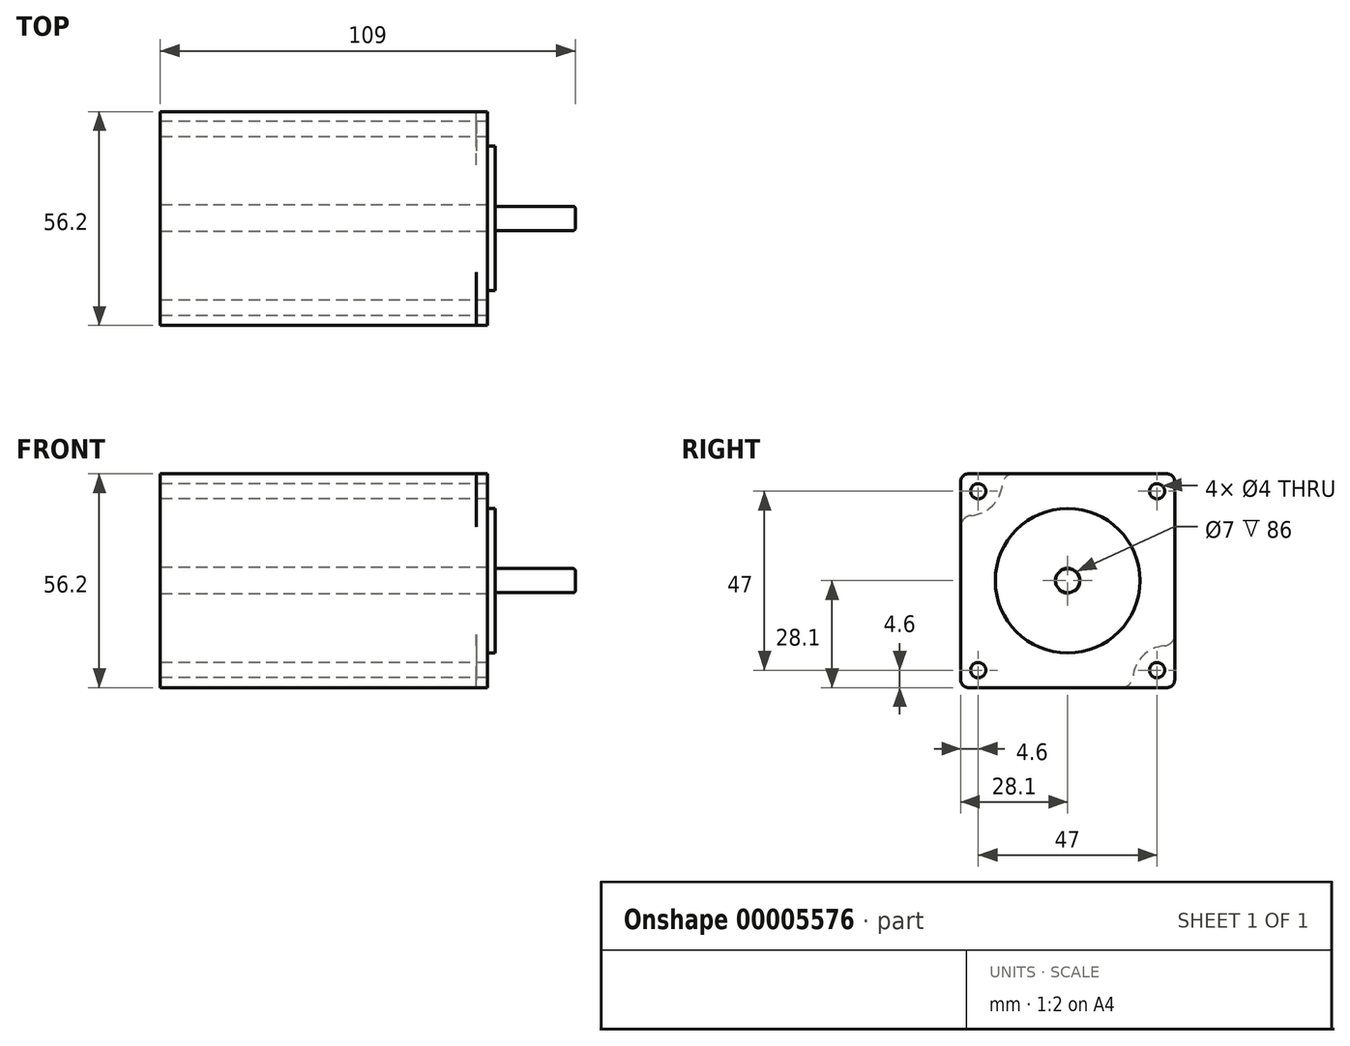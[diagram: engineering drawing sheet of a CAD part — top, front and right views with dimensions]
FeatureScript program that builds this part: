
annotation { "Feature Type Name" : "Feature", "Feature Type Description" : "" }
export const myFeature = defineFeature(function(context is Context, id is Id, definition is map)
    precondition{}
    {
        {
            var Q0;
            Q0=qCreatedBy(makeId("Right.planeOp"),FACE);
            var sketch = newSketch(context, id + "F0", { "sketchPlane" : qUnion([Q0])});
            skLineSegment(sketch, "E0.bottom", {"start": v(-26.1, 28.1) * mm, "end": v(26.1, 28.1) * mm});
            skLineSegment(sketch, "E0.top", {"start": v(-26.1, -28.1) * mm, "end": v(26.1, -28.1) * mm});
            skLineSegment(sketch, "E0.left", {"start": v(-28.1, 26.1) * mm, "end": v(-28.1, -26.1) * mm});
            skLineSegment(sketch, "E0.right", {"start": v(28.1, 26.1) * mm, "end": v(28.1, -26.1) * mm});
            skLineSegment(sketch, "E1", {"start": v(-28.1, 0) * mm, "end": v(28.1, 0) * mm, "construction": true});
            skLineSegment(sketch, "E2", {"start": v(0, 28.1) * mm, "end": v(0, -28.1) * mm, "construction": true});
            skCircle(sketch, "E3", {"center": v(-23.5, 23.5) * mm, "radius": 2 * mm});
            skCircle(sketch, "E4.0.MirrorC", {"center": v(23.5, 23.5) * mm, "radius": 2 * mm});
            skCircle(sketch, "E5.0.MirrorC", {"center": v(23.5, -23.5) * mm, "radius": 2 * mm});
            skCircle(sketch, "E6.0.MirrorC", {"center": v(-23.5, -23.5) * mm, "radius": 2 * mm});
            skCircle(sketch, "E7", {"center": v(0, 0) * mm, "radius": 19 * mm, "construction": true});
            skPoint(sketch, "E8.visualSharp", {"position": v(-28.1, 28.1) * mm});
            skArc(sketch, "E8.filletArc", {"start": v(-26.1, 28.1) * mm, "mid": v(-27.51, 27.51) * mm, "end": v(-28.1, 26.1) * mm});
            skPoint(sketch, "E9.visualSharp", {"position": v(28.1, 28.1) * mm});
            skArc(sketch, "E9.filletArc", {"start": v(28.1, 26.1) * mm, "mid": v(27.51, 27.51) * mm, "end": v(26.1, 28.1) * mm});
            skPoint(sketch, "E10.visualSharp", {"position": v(28.1, -28.1) * mm});
            skArc(sketch, "E10.filletArc", {"start": v(26.1, -28.1) * mm, "mid": v(27.51, -27.51) * mm, "end": v(28.1, -26.1) * mm});
            skPoint(sketch, "E11.visualSharp", {"position": v(-28.1, -28.1) * mm});
            skArc(sketch, "E11.filletArc", {"start": v(-28.1, -26.1) * mm, "mid": v(-27.51, -27.51) * mm, "end": v(-26.1, -28.1) * mm});
            skLineSegment(sketch, "E12", {"start": v(23.5, 23.5) * mm, "end": v(-23.5, 23.5) * mm, "construction": true});
            skLineSegment(sketch, "E13", {"start": v(-23.5, 23.5) * mm, "end": v(-23.5, -23.5) * mm, "construction": true});
            skLineSegment(sketch, "E14", {"start": v(28.1, 28.1) * mm, "end": v(-28.1, 28.1) * mm, "construction": true});
            skLineSegment(sketch, "E15", {"start": v(-28.1, -28.1) * mm, "end": v(-28.1, 28.1) * mm, "construction": true});
            skCircle(sketch, "E16", {"center": v(0, 0) * mm, "radius": 3.5 * mm});
            skSolve(sketch);
        }
        {
            var Q0;
            Q0=makeQuery(id+"F0.imprint","IMPRINT",FACE,{"disambiguationData":[TD([[makeQuery(id+"F0.imprint","IMPRINT",EDGE,{"derivedFrom":sQuery(id+"F0.wireOp",EDGE,"E0.bottom")}),-1.0]])]});
            extrude(context, id + "F1", {"entities" : qUnion([Q0]), "depth" : 86 * mm});
        }
        {
            var Q0;
            Q0=makeQuery(id+"F1.opExtrude","CAP_FACE",FACE,{"disambiguationData":[OSD([sQuery(id+"F0.wireOp",EDGE,"E0.bottom"),sQuery(id+"F0.wireOp",EDGE,"E0.top"),sQuery(id+"F0.wireOp",EDGE,"E0.left"),sQuery(id+"F0.wireOp",EDGE,"E0.right"),sQuery(id+"F0.wireOp",EDGE,"E3"),sQuery(id+"F0.wireOp",EDGE,"E4.0.MirrorC"),sQuery(id+"F0.wireOp",EDGE,"E5.0.MirrorC"),sQuery(id+"F0.wireOp",EDGE,"E6.0.MirrorC"),sQuery(id+"F0.wireOp",EDGE,"E8.filletArc"),sQuery(id+"F0.wireOp",EDGE,"E9.filletArc"),sQuery(id+"F0.wireOp",EDGE,"E10.filletArc"),sQuery(id+"F0.wireOp",EDGE,"E11.filletArc"),sQuery(id+"F0.wireOp",EDGE,"E16")])],"isStart":false});
            var sketch = newSketch(context, id + "F2", { "sketchPlane" : qUnion([Q0])});
            skCircle(sketch, "E17", {"center": v(0, 0) * mm, "radius": 19 * mm});
            skSolve(sketch);
        }
        {
            var Q0;
            {var subQ0=makeQuery(id+"F2.imprint","IMPRINT",EDGE,{"derivedFrom":makeQuery(id+"F1.opExtrude","CAP_EDGE",EDGE,{"disambiguationData":[OSD([sQuery(id+"F0.wireOp",EDGE,"E16")])],"isStart":false})});Q0=qUnion([makeQuery(id+"F2.imprint","IMPRINT",FACE,{"disambiguationData":[TD([[subQ0,1.0]])]}),makeQuery(id+"F2.imprint","IMPRINT",FACE,{"disambiguationData":[TD([[makeQuery(id+"F2.imprint","IMPRINT",EDGE,{"derivedFrom":sQuery(id+"F2.wireOp",EDGE,"E17")}),1.0]])]})]);}
            extrude(context, id + "F3", {"entities" : qUnion([Q0]), "operationType" : NewBodyOperationType.ADD, "depth" : 2 * mm});
        }
        {
            var Q0;
            Q0=makeQuery(id+"F3.opExtrude","CAP_FACE",FACE,{"disambiguationData":[OSD([sQuery(id+"F2.wireOp",EDGE,"E17")])],"isStart":false});
            var sketch = newSketch(context, id + "F4", { "sketchPlane" : qUnion([Q0])});
            skCircle(sketch, "E18", {"center": v(0, 0) * mm, "radius": 3.17 * mm});
            skSolve(sketch);
        }
        {
            var Q0;
            Q0=makeQuery(id+"F4.imprint","IMPRINT",FACE,{"disambiguationData":[TD([[makeQuery(id+"F4.imprint","IMPRINT",EDGE,{"derivedFrom":sQuery(id+"F4.wireOp",EDGE,"E18")}),1.0]])]});
            extrude(context, id + "F5", {"entities" : qUnion([Q0]), "operationType" : NewBodyOperationType.ADD, "depth" : 21 * mm});
        }
        {
            var Q0;
            Q0=makeQuery(id+"F5.opExtrude","CAP_EDGE",EDGE,{"disambiguationData":[OSD([sQuery(id+"F4.wireOp",EDGE,"E18")])],"isStart":false});
            fillet(context, id + "F6", {"entities" : qUnion([Q0]), "radius" : 0.5 * mm, "tangentPropagation" : true, "allowEdgeOverflow" : false});
        }
        {
            var Q0;
            Q0=makeQuery(id+"F1.opExtrude","CAP_FACE",FACE,{"disambiguationData":[OSD([sQuery(id+"F0.wireOp",EDGE,"E0.bottom"),sQuery(id+"F0.wireOp",EDGE,"E0.top"),sQuery(id+"F0.wireOp",EDGE,"E0.left"),sQuery(id+"F0.wireOp",EDGE,"E0.right"),sQuery(id+"F0.wireOp",EDGE,"E3"),sQuery(id+"F0.wireOp",EDGE,"E4.0.MirrorC"),sQuery(id+"F0.wireOp",EDGE,"E5.0.MirrorC"),sQuery(id+"F0.wireOp",EDGE,"E6.0.MirrorC"),sQuery(id+"F0.wireOp",EDGE,"E8.filletArc"),sQuery(id+"F0.wireOp",EDGE,"E9.filletArc"),sQuery(id+"F0.wireOp",EDGE,"E10.filletArc"),sQuery(id+"F0.wireOp",EDGE,"E11.filletArc"),sQuery(id+"F0.wireOp",EDGE,"E16")])],"isStart":false});
            cPlane(context, id + "F7", {"entities" : qUnion([Q0]), "cplaneType" : CPlaneType.OFFSET, "offset" : 3 * mm, "oppositeDirection" : true, "width" : 150 * mm, "height" : 150 * mm});
        }
        {
            var Q0;
            Q0=qCreatedBy(id+"F7.planeOp",FACE);
            var sketch = newSketch(context, id + "F8", { "sketchPlane" : qUnion([Q0])});
            skCircle(sketch, "E19", {"center": v(-26.1, 26.1) * mm, "radius": 9 * mm});
            skCircle(sketch, "E20.0.MirrorC", {"center": v(26.1, 26.1) * mm, "radius": 9 * mm});
            skCircle(sketch, "E21.0.MirrorC", {"center": v(-26.1, -26.1) * mm, "radius": 9 * mm});
            skCircle(sketch, "E22.0.MirrorC", {"center": v(26.1, -26.1) * mm, "radius": 9 * mm});
            skSolve(sketch);
        }
        {
            var Q0;
            {Q0=qUnion([makeQuery(id+"F8.imprint","IMPRINT",FACE,{"disambiguationData":[TD([[makeQuery(id+"F8.imprint","IMPRINT",EDGE,{"derivedFrom":sQuery(id+"F8.wireOp",EDGE,"E19")}),1.0]])]}),makeQuery(id+"F8.imprint","IMPRINT",FACE,{"disambiguationData":[TD([[makeQuery(id+"F8.imprint","IMPRINT",EDGE,{"derivedFrom":sQuery(id+"F8.wireOp",EDGE,"E20.0.MirrorC")}),-1.0]])]}),makeQuery(id+"F8.imprint","IMPRINT",FACE,{"disambiguationData":[TD([[makeQuery(id+"F8.imprint","IMPRINT",EDGE,{"derivedFrom":sQuery(id+"F8.wireOp",EDGE,"E21.0.MirrorC")}),-1.0]])]}),makeQuery(id+"F8.imprint","IMPRINT",FACE,{"disambiguationData":[TD([[makeQuery(id+"F8.imprint","IMPRINT",EDGE,{"derivedFrom":sQuery(id+"F8.wireOp",EDGE,"E22.0.MirrorC")}),1.0]])]})]);}
            var Q1;
            Q1=makeQuery(id+"F1.opExtrude","CAP_FACE",FACE,{"disambiguationData":[OSD([sQuery(id+"F0.wireOp",EDGE,"E0.bottom"),sQuery(id+"F0.wireOp",EDGE,"E0.top"),sQuery(id+"F0.wireOp",EDGE,"E0.left"),sQuery(id+"F0.wireOp",EDGE,"E0.right"),sQuery(id+"F0.wireOp",EDGE,"E3"),sQuery(id+"F0.wireOp",EDGE,"E4.0.MirrorC"),sQuery(id+"F0.wireOp",EDGE,"E5.0.MirrorC"),sQuery(id+"F0.wireOp",EDGE,"E6.0.MirrorC"),sQuery(id+"F0.wireOp",EDGE,"E8.filletArc"),sQuery(id+"F0.wireOp",EDGE,"E9.filletArc"),sQuery(id+"F0.wireOp",EDGE,"E10.filletArc"),sQuery(id+"F0.wireOp",EDGE,"E11.filletArc"),sQuery(id+"F0.wireOp",EDGE,"E16")])],"isStart":true});
            extrude(context, id + "F9", {"entities" : qUnion([Q0]), "operationType" : NewBodyOperationType.REMOVE, "endBound" : BoundingType.UP_TO_SURFACE, "oppositeDirection" : true, "endBoundEntityFace" : qUnion([Q1]), "depth" : 25 * mm});
        }
        {
            var Q0;
            Q0=makeQuery(id+"F9.boolean.opBoolean","INTERSECT",EDGE,{"derivedFrom":[makeQuery(id+"F1.opExtrude","SWEPT_FACE",FACE,{"disambiguationData":[OSD([sQuery(id+"F0.wireOp",EDGE,"E0.bottom")])]}),makeQuery(id+"F9.opExtrude","SWEPT_FACE",FACE,{"disambiguationData":[OSD([sQuery(id+"F8.wireOp",EDGE,"E20.0.MirrorC")])]})]});
            var Q1;
            Q1=makeQuery(id+"F9.boolean.opBoolean","INTERSECT",EDGE,{"derivedFrom":[makeQuery(id+"F1.opExtrude","SWEPT_FACE",FACE,{"disambiguationData":[OSD([sQuery(id+"F0.wireOp",EDGE,"E0.right")])]}),makeQuery(id+"F9.opExtrude","SWEPT_FACE",FACE,{"disambiguationData":[OSD([sQuery(id+"F8.wireOp",EDGE,"E20.0.MirrorC")])]})]});
            var Q2;
            Q2=makeQuery(id+"F9.boolean.opBoolean","INTERSECT",EDGE,{"derivedFrom":[makeQuery(id+"F1.opExtrude","SWEPT_FACE",FACE,{"disambiguationData":[OSD([sQuery(id+"F0.wireOp",EDGE,"E0.bottom")])]}),makeQuery(id+"F9.opExtrude","SWEPT_FACE",FACE,{"disambiguationData":[OSD([sQuery(id+"F8.wireOp",EDGE,"E19")])]})]});
            var Q3;
            Q3=makeQuery(id+"F9.boolean.opBoolean","INTERSECT",EDGE,{"derivedFrom":[makeQuery(id+"F1.opExtrude","SWEPT_FACE",FACE,{"disambiguationData":[OSD([sQuery(id+"F0.wireOp",EDGE,"E0.left")])]}),makeQuery(id+"F9.opExtrude","SWEPT_FACE",FACE,{"disambiguationData":[OSD([sQuery(id+"F8.wireOp",EDGE,"E19")])]})]});
            var Q4;
            Q4=makeQuery(id+"F9.boolean.opBoolean","INTERSECT",EDGE,{"derivedFrom":[makeQuery(id+"F1.opExtrude","SWEPT_FACE",FACE,{"disambiguationData":[OSD([sQuery(id+"F0.wireOp",EDGE,"E0.left")])]}),makeQuery(id+"F9.opExtrude","SWEPT_FACE",FACE,{"disambiguationData":[OSD([sQuery(id+"F8.wireOp",EDGE,"E21.0.MirrorC")])]})]});
            var Q5;
            Q5=makeQuery(id+"F9.boolean.opBoolean","INTERSECT",EDGE,{"derivedFrom":[makeQuery(id+"F1.opExtrude","SWEPT_FACE",FACE,{"disambiguationData":[OSD([sQuery(id+"F0.wireOp",EDGE,"E0.top")])]}),makeQuery(id+"F9.opExtrude","SWEPT_FACE",FACE,{"disambiguationData":[OSD([sQuery(id+"F8.wireOp",EDGE,"E21.0.MirrorC")])]})]});
            var Q6;
            Q6=makeQuery(id+"F9.boolean.opBoolean","INTERSECT",EDGE,{"derivedFrom":[makeQuery(id+"F1.opExtrude","SWEPT_FACE",FACE,{"disambiguationData":[OSD([sQuery(id+"F0.wireOp",EDGE,"E0.top")])]}),makeQuery(id+"F9.opExtrude","SWEPT_FACE",FACE,{"disambiguationData":[OSD([sQuery(id+"F8.wireOp",EDGE,"E22.0.MirrorC")])]})]});
            var Q7;
            Q7=makeQuery(id+"F9.boolean.opBoolean","INTERSECT",EDGE,{"derivedFrom":[makeQuery(id+"F1.opExtrude","SWEPT_FACE",FACE,{"disambiguationData":[OSD([sQuery(id+"F0.wireOp",EDGE,"E0.right")])]}),makeQuery(id+"F9.opExtrude","SWEPT_FACE",FACE,{"disambiguationData":[OSD([sQuery(id+"F8.wireOp",EDGE,"E22.0.MirrorC")])]})]});
            fillet(context, id + "F10", {"entities" : qUnion([Q0, Q1, Q2, Q3, Q4, Q5, Q6, Q7]), "radius" : 3 * mm, "tangentPropagation" : true, "allowEdgeOverflow" : false});
        }
    });
